FCSTD DOCUMENT  (FreeCAD 0.21R33321 (Git))
Label: 20230531-sunroom-layout
License: All rights reserved
LicenseURL: http://en.wikipedia.org/wiki/All_rights_reserved
objects: Part::Part2DObjectPython×75, Part::FeaturePython×35, App::DocumentObjectGroup×13, App::MeasureDistance×1, Spreadsheet::Sheet×1, App::GeometryPython×1
note: 111 computed .brp shape members not serialized (recipe doc carries the construction recipe); baked Part::Feature solids carry a one-line shape summary decoded from their .brp

FEATURE [Part::Part2DObjectPython] Rectangle001  label="Rect-sec1"  # Draft 2D object (typed FeaturePython)
  Area = 800000
  ChamferSize = 0
  Columns = 1
  FilletRadius = 0
  Height = 400
  Length = 2000
  MakeFace = true
  Placement = pos=(-5613.61,2200,0) rot=(0,0,1;0rad)
  Rows = 1
FEATURE [Part::FeaturePython] Structure001  label="fail"  # Arch/BIM 7 (typed FeaturePython)
  BaseMirror = false
  BaseOffsetX = 0
  BaseOffsetY = 0
  BasePerpendicularToTool = false
  BaseRotation = -21
  ComputedLength = 6000
  FaceMaker = 0
  Height = 64
  HorizontalArea = 4096
  IfcData = attributes={"GlobalId": {"name": "GlobalId", "type": "IfcGloballyUniqueId", "is_enum": false, "enum_values": []}, "Description": {"... (+475 chars omitted),+1 more (map truncated)
  IfcType = 7
  Length = 6000
  MoveBase = false
  MoveWithHost = false
  Nodes = (2) [(-3.54371e-32,-1.11022e-15,8.32667e-16),(6000,-1.11022e-15,8.32667e-16)]
  NodesOffset = 0
  Normal = (0,0,0)
  PerimeterLength = 256
  Placement = pos=(-5368,2460,5000) rot=(0,1,0;1.5708rad)
  PredefinedType = 0
  Profile = IPE120
  ToolOffsetFirst = 0
  ToolOffsetLast = 0
  VerticalArea = 1536000
  Width = 64
  expr: Profile = Spreadsheet.vertcoltype
FEATURE [Part::FeaturePython] Wall  label="NorthWall1-400mm"  # Arch/BIM 166 (typed FeaturePython)
  Align = 2
  Area = 0
  Base = -> Rectangle001
  BlockHeight = 0
  BlockLength = 0
  CountBroken = 0
  CountEntire = 0
  Face = 0
  Height = 3000
  HorizontalArea = 800000
  IfcData = attributes={"GlobalId": {"name": "GlobalId", "type": "IfcGloballyUniqueId", "is_enum": false, "enum_values": []}, "Description": {"... (+533 chars omitted),+1 more (map truncated)
  IfcType = 166
  Joint = 0
  Length = 0
  MakeBlocks = false
  MoveBase = false
  MoveWithHost = false
  Normal = (0,0,0)
  OffsetFirst = 0
  OffsetSecond = 0
  PerimeterLength = 4800
  Placement = pos=(0,0,-600) rot=(0,0,1;0rad)
  PredefinedType = 0
  VerticalArea = 1.44e+07
  Width = 200
FEATURE [App::MeasureDistance] Distance  label="Distance: 2363.01 mm"
  Distance = 2398.43
  P1 = (-3738.2,2140,2600)
  P2 = (-3709.77,2140,4998.26)
FEATURE [Spreadsheet::Sheet] Spreadsheet  label="S"
  cells = A1=BaseHeight; B1(BaseHeight)==5200 mm; A2=BaseLength; B2(BaseLength)==11000 mm; A3=BaseSlabThickness; B3(BaseSlabThickness)==200 mm; A4=ColHeight; B4(ColHeight)==6000 mm; A5=NorthWallThickness; B5(NorthWallThickness)==400 mm; A6=SouthWallThickness; B6(SouthWallThickness)==200 mm; A7=LaundryRoomWidth; B7(LaundryRoomWidth)==3 m; A8=LaundryRoomDepth; B8(LaundryRoomDepth)==3 m; A9=col1xpos; B9(col1xpos)==-BaseLength / 2 + 100 mm; A10=col1ypos; B10(col1ypos)==BaseHeight / 2 - NorthWallThickness / 2; A11=col1xposIPE; B11(col1xposIPE)==col1xpos + 32 mm; A12=col1yposIPE; B12(col1yposIPE)==col1ypos + 60 mm; A13=colwidth; B13(colwidth)==64 mm; A14=colheight; B14(collength)==120 mm; A15=vertcoltype; B15(vertcoltype)=IPE120
FEATURE [Part::Part2DObjectPython] Rectangle003  label="NorthWallRect"  # Draft 2D object (typed FeaturePython)
  Area = 3320000
  ChamferSize = 0
  Columns = 1
  FilletRadius = 0
  Height = 400
  Length = 8300
  MakeFace = true
  Placement = pos=(-5500,2200,0) rot=(0,0,1;0rad)
  Rows = 1
  expr: .Placement.Base.x = -Spreadsheet.BaseLength / 2
  expr: .Placement.Base.y = Spreadsheet.BaseHeight / 2 - Spreadsheet.NorthWallThickness
  expr: Height = Spreadsheet.NorthWallThickness
  expr: Length = Spreadsheet.BaseLength - 3 m + 300 mm
FEATURE [Part::Part2DObjectPython] Rectangle004  label="SouthWallRect"  # Draft 2D object (typed FeaturePython)
  Area = 2200000
  ChamferSize = 0
  Columns = 1
  FilletRadius = 0
  Height = 200
  Length = 11000
  MakeFace = true
  Placement = pos=(-5500,-2600,0) rot=(0,0,1;0rad)
  Rows = 1
  expr: .Placement.Base.x = -Spreadsheet.BaseLength / 2
  expr: .Placement.Base.y = -Spreadsheet.BaseHeight / 2
  expr: Height = Spreadsheet.SouthWallThickness
  expr: Length = Spreadsheet.BaseLength
FEATURE [Part::Part2DObjectPython] Rectangle005  label="NorthColPosRect"  # Draft 2D object (typed FeaturePython)
  Area = 960000
  ChamferSize = 0
  Columns = 1
  FilletRadius = 0
  Height = 120
  Length = 8000
  MakeFace = true
  Placement = pos=(-5500,2400,0) rot=(0,0,1;0rad)
  Rows = 1
  expr: .Placement.Base.x = -Spreadsheet.BaseLength / 2
  expr: .Placement.Base.y = Spreadsheet.BaseHeight / 2 - Spreadsheet.NorthWallThickness / 2
FEATURE [Part::Part2DObjectPython] Rectangle006  label="WestWallRect"  # Draft 2D object (typed FeaturePython)
  Area = 920000
  ChamferSize = 0
  Columns = 1
  FilletRadius = 0
  Height = 4600
  Length = 200
  MakeFace = true
  Placement = pos=(-5500,-2400,0) rot=(0,0,1;0rad)
  Rows = 1
  expr: Height = Spreadsheet.BaseHeight - Spreadsheet.NorthWallThickness - Spreadsheet.SouthWallThickness
  expr: Length = Spreadsheet.SouthWallThickness
FEATURE [Part::Part2DObjectPython] Rectangle007  label="Col1Rect"  # Draft 2D object (typed FeaturePython)
  Area = 7680
  ChamferSize = 0
  Columns = 1
  FilletRadius = 0
  Height = 120
  Length = 64
  MakeFace = true
  Placement = pos=(-5400,2400,0) rot=(0,0,1;0rad)
  Rows = 1
  expr: .Placement.Base.x = Spreadsheet.col1xpos
  expr: .Placement.Base.y = Spreadsheet.col1ypos
  expr: Height = Spreadsheet.collength
  expr: Length = Spreadsheet.colwidth
FEATURE [Part::Part2DObjectPython] Clone2D  label="Col2Rect (2D)"  # Draft 2D object (typed FeaturePython)
  Fuse = false
  Objects = -> [Rectangle007]
  Placement = pos=(-4400,2400,0) rot=(0,0,1;0rad)
  Scale = (1,1,1)
  expr: .Placement.Base.x = Spreadsheet.col1xpos + 1000 mm
  expr: .Placement.Base.y = Spreadsheet.col1ypos
FEATURE [Part::Part2DObjectPython] Clone2D001  label="Col3Rect (2D)"  # Draft 2D object (typed FeaturePython)
  Fuse = false
  Objects = -> [Rectangle007]
  Placement = pos=(-3400,2400,0) rot=(0,0,1;0rad)
  Scale = (1,1,1)
  expr: .Placement.Base.x = Spreadsheet.col1xpos + 2000 mm
FEATURE [Part::Part2DObjectPython] Clone2D002  label="Col4Rect (2D)"  # Draft 2D object (typed FeaturePython)
  Fuse = false
  Objects = -> [Rectangle007]
  Placement = pos=(-2400,2400,0) rot=(0,0,1;0rad)
  Scale = (1,1,1)
  expr: .Placement.Base.x = Spreadsheet.col1xpos + 3000 mm
  expr: .Placement.Base.y = Spreadsheet.col1ypos
FEATURE [Part::Part2DObjectPython] Clone2D003  label="Col5Rect (2D)"  # Draft 2D object (typed FeaturePython)
  Fuse = false
  Objects = -> [Rectangle007]
  Placement = pos=(-1400,2400,0) rot=(0,0,1;0rad)
  Scale = (1,1,1)
  expr: .Placement.Base.x = Spreadsheet.col1xpos + 4000 mm
  expr: .Placement.Base.y = Spreadsheet.col1ypos
FEATURE [Part::Part2DObjectPython] Clone2D004  label="Col7Rect (2D)"  # Draft 2D object (typed FeaturePython)
  Fuse = false
  Objects = -> [Rectangle007]
  Placement = pos=(600,2400,0) rot=(0,0,1;0rad)
  Scale = (1,1,1)
  expr: .Placement.Base.x = Spreadsheet.col1xpos + 6000 mm
  expr: .Placement.Base.y = Spreadsheet.col1ypos
FEATURE [Part::Part2DObjectPython] Clone2D005  label="Col6Rect (2D)"  # Draft 2D object (typed FeaturePython)
  Fuse = false
  Objects = -> [Rectangle007]
  Placement = pos=(-400,2400,0) rot=(0,0,1;0rad)
  Scale = (1,1,1)
  expr: .Placement.Base.x = Spreadsheet.col1xpos + 5000 mm
  expr: .Placement.Base.y = Spreadsheet.col1ypos
FEATURE [Part::Part2DObjectPython] Clone2D006  label="Col8Rect (2D)"  # Draft 2D object (typed FeaturePython)
  Fuse = false
  Objects = -> [Rectangle007]
  Placement = pos=(1600,2400,0) rot=(0,0,1;0rad)
  Scale = (1,1,1)
  expr: .Placement.Base.x = Spreadsheet.col1xpos + 7000 mm
  expr: .Placement.Base.y = Spreadsheet.col1ypos
FEATURE [Part::Part2DObjectPython] Rectangle008  label="LaundryRoomRect"  # Draft 2D object (typed FeaturePython)
  Area = 9000000
  ChamferSize = 0
  Columns = 1
  FilletRadius = 0
  Height = 3000
  Length = 3000
  MakeFace = true
  Placement = pos=(2500,2600,0) rot=(0,0,1;0rad)
  Rows = 1
  expr: .Placement.Base.x = 2500
  expr: Height = Spreadsheet.LaundryRoomDepth
  expr: Length = Spreadsheet.LaundryRoomDepth
FEATURE [Part::Part2DObjectPython] Clone2D007  label="Col9Rect (2D)"  # Draft 2D object (typed FeaturePython)
  Fuse = false
  Objects = -> [Rectangle007]
  Placement = pos=(2602.84,2400.21,0) rot=(0,0,1;0rad)
  Scale = (1,1,1)
FEATURE [App::DocumentObjectGroup] Group001  label="RectN"
  Group = -> [Rectangle007,Clone2D,Clone2D001,Clone2D002,Clone2D003,Clone2D005,Clone2D004,Clone2D006,Clone2D007]
FEATURE [Part::Part2DObjectPython] Clone2D008  label="Col10Rect (2D)"  # Draft 2D object (typed FeaturePython)
  Fuse = false
  Objects = -> [Clone2D007]
  Placement = pos=(2720,3400,0) rot=(0,0,1;1.5708rad)
  Scale = (1,1,1)
  expr: .Placement.Base.x = 2720 mm
  expr: .Placement.Base.y = 2400 mm + 1000 mm
FEATURE [Part::Part2DObjectPython] IPE120005  # Draft 2D object (typed FeaturePython)
  FlangeThickness = 6.3
  Height = 120
  WebThickness = 4.4
  Width = 64
FEATURE [Part::FeaturePython] Structure006  label="Col5"  # Arch/BIM 24 (typed FeaturePython)
  Base = -> IPE120005
  BaseMirror = false
  BaseOffsetX = 0
  BaseOffsetY = 0
  BasePerpendicularToTool = false
  BaseRotation = 0
  ComputedLength = 6000
  FaceMaker = 0
  Height = 6000
  HorizontalArea = 1278.96
  IfcData = attributes={"GlobalId": {"name": "GlobalId", "type": "IfcGloballyUniqueId", "is_enum": false, "enum_values": []}, "Description": {"... (+438 chars omitted),+1 more (map truncated)
  IfcType = 24
  Length = 120
  MoveBase = false
  MoveWithHost = false
  Nodes = (2) [(0,-1.61713e-15,0),(0,-1.61713e-15,6000)]
  NodesOffset = 0
  Normal = (0,0,0)
  PerimeterLength = 487.2
  Placement = pos=(-1368,2460,-1000) rot=(0,0,1;0rad)
  PredefinedType = 0
  Profile = IPE120
  ToolOffsetFirst = 0
  ToolOffsetLast = 0
  VerticalArea = 2923200
  Width = 64
  expr: .Placement.Base.x = Spreadsheet.col1xposIPE + 4000 mm
  expr: .Placement.Base.y = Spreadsheet.col1yposIPE
FEATURE [Part::Part2DObjectPython] IPE120006  # Draft 2D object (typed FeaturePython)
  FlangeThickness = 6.3
  Height = 120
  WebThickness = 4.4
  Width = 64
FEATURE [Part::FeaturePython] Structure007  label="Col6"  # Arch/BIM 24 (typed FeaturePython)
  Base = -> IPE120006
  BaseMirror = false
  BaseOffsetX = 0
  BaseOffsetY = 0
  BasePerpendicularToTool = false
  BaseRotation = 0
  ComputedLength = 6000
  FaceMaker = 0
  Height = 6000
  HorizontalArea = 1278.96
  IfcData = attributes={"GlobalId": {"name": "GlobalId", "type": "IfcGloballyUniqueId", "is_enum": false, "enum_values": []}, "Description": {"... (+438 chars omitted),+1 more (map truncated)
  IfcType = 24
  Length = 120
  MoveBase = false
  MoveWithHost = false
  Nodes = (2) [(0,-1.61713e-15,0),(0,-1.61713e-15,6000)]
  NodesOffset = 0
  Normal = (0,0,0)
  PerimeterLength = 487.2
  Placement = pos=(-368,2460,-1000) rot=(0,0,1;0rad)
  PredefinedType = 0
  Profile = IPE120
  ToolOffsetFirst = 0
  ToolOffsetLast = 0
  VerticalArea = 2923200
  Width = 64
  expr: .Placement.Base.x = Spreadsheet.col1xposIPE + 5000 mm
  expr: .Placement.Base.y = Spreadsheet.col1yposIPE
FEATURE [Part::Part2DObjectPython] IPE120007  # Draft 2D object (typed FeaturePython)
  FlangeThickness = 6.3
  Height = 120
  WebThickness = 4.4
  Width = 64
FEATURE [Part::FeaturePython] Structure008  label="Col7"  # Arch/BIM 24 (typed FeaturePython)
  Base = -> IPE120007
  BaseMirror = false
  BaseOffsetX = 0
  BaseOffsetY = 0
  BasePerpendicularToTool = false
  BaseRotation = 0
  ComputedLength = 6000
  FaceMaker = 0
  Height = 6000
  HorizontalArea = 1278.96
  IfcData = attributes={"GlobalId": {"name": "GlobalId", "type": "IfcGloballyUniqueId", "is_enum": false, "enum_values": []}, "Description": {"... (+438 chars omitted),+1 more (map truncated)
  IfcType = 24
  Length = 120
  MoveBase = false
  MoveWithHost = false
  Nodes = (2) [(0,-1.61713e-15,0),(0,-1.61713e-15,6000)]
  NodesOffset = 0
  Normal = (0,0,0)
  PerimeterLength = 487.2
  Placement = pos=(632,2460,-1000) rot=(0,0,1;0rad)
  PredefinedType = 0
  Profile = IPE120
  ToolOffsetFirst = 0
  ToolOffsetLast = 0
  VerticalArea = 2923200
  Width = 64
  expr: .Placement.Base.x = Spreadsheet.col1xposIPE + 6000 mm
  expr: .Placement.Base.y = Spreadsheet.col1yposIPE
FEATURE [Part::Part2DObjectPython] IPE120008  # Draft 2D object (typed FeaturePython)
  FlangeThickness = 6.3
  Height = 120
  WebThickness = 4.4
  Width = 64
FEATURE [Part::FeaturePython] Structure009  label="Col8"  # Arch/BIM 24 (typed FeaturePython)
  Base = -> IPE120008
  BaseMirror = false
  BaseOffsetX = 0
  BaseOffsetY = 0
  BasePerpendicularToTool = false
  BaseRotation = 0
  ComputedLength = 6000
  FaceMaker = 0
  Height = 6000
  HorizontalArea = 1278.96
  IfcData = attributes={"GlobalId": {"name": "GlobalId", "type": "IfcGloballyUniqueId", "is_enum": false, "enum_values": []}, "Description": {"... (+438 chars omitted),+1 more (map truncated)
  IfcType = 24
  Length = 120
  MoveBase = false
  MoveWithHost = false
  Nodes = (2) [(0,-1.61713e-15,0),(0,-1.61713e-15,6000)]
  NodesOffset = 0
  Normal = (0,0,0)
  PerimeterLength = 487.2
  Placement = pos=(1632,2460,-1000) rot=(0,0,1;0rad)
  PredefinedType = 0
  Profile = IPE120
  ToolOffsetFirst = 0
  ToolOffsetLast = 0
  VerticalArea = 2923200
  Width = 64
  expr: .Placement.Base.x = Spreadsheet.col1xposIPE + 7000 mm
  expr: .Placement.Base.y = Spreadsheet.col1yposIPE
FEATURE [Part::Part2DObjectPython] IPE120009  # Draft 2D object (typed FeaturePython)
  FlangeThickness = 6.3
  Height = 120
  WebThickness = 4.4
  Width = 64
FEATURE [Part::FeaturePython] Structure010  label="Col9"  # Arch/BIM 24 (typed FeaturePython)
  Base = -> IPE120009
  BaseMirror = false
  BaseOffsetX = 0
  BaseOffsetY = 0
  BasePerpendicularToTool = false
  BaseRotation = 0
  ComputedLength = 6000
  FaceMaker = 0
  Height = 6000
  HorizontalArea = 1278.96
  IfcData = attributes={"GlobalId": {"name": "GlobalId", "type": "IfcGloballyUniqueId", "is_enum": false, "enum_values": []}, "Description": {"... (+438 chars omitted),+1 more (map truncated)
  IfcType = 24
  Length = 120
  MoveBase = false
  MoveWithHost = false
  Nodes = (2) [(0,-1.61713e-15,0),(0,-1.61713e-15,6000)]
  NodesOffset = 0
  Normal = (0,0,0)
  PerimeterLength = 487.2
  Placement = pos=(2634.76,2460.15,-1000) rot=(0,0,1;0rad)
  PredefinedType = 0
  Profile = IPE120
  ToolOffsetFirst = 0
  ToolOffsetLast = 0
  VerticalArea = 2923200
  Width = 64
FEATURE [Part::Part2DObjectPython] Rectangle009  label="LaundryWallWestRect"  # Draft 2D object (typed FeaturePython)
  Area = 900000
  ChamferSize = 0
  Columns = 1
  FilletRadius = 0
  Height = 3000
  Length = 300
  MakeFace = true
  Placement = pos=(2500.39,2600,0) rot=(0,0,1;0rad)
  Rows = 1
  expr: Height = Spreadsheet.LaundryRoomDepth
FEATURE [Part::Part2DObjectPython] Clone2D009  label="Col11Rect (2D)"  # Draft 2D object (typed FeaturePython)
  Fuse = false
  Objects = -> [Clone2D008]
  Placement = pos=(2720,4400,0) rot=(0,0,1;1.5708rad)
  Scale = (1,1,1)
  expr: .Placement.Base.y = 2400 mm + 2000 mm
FEATURE [Part::Part2DObjectPython] Clone2D010  label="Col12Rect (2D)"  # Draft 2D object (typed FeaturePython)
  Fuse = false
  Objects = -> [Clone2D009]
  Placement = pos=(2720,5400,0) rot=(0,0,1;1.5708rad)
  Scale = (1,1,1)
  expr: .Placement.Base.y = 2400 mm + 3000 mm
FEATURE [Part::Part2DObjectPython] Rectangle010  label="LaundryWallEastRect"  # Draft 2D object (typed FeaturePython)
  Area = 600000
  ChamferSize = 0
  Columns = 1
  FilletRadius = 0
  Height = 3000
  Length = 200
  MakeFace = true
  Placement = pos=(5300,2600,0) rot=(0,0,1;0rad)
  Rows = 1
  expr: Height = Spreadsheet.LaundryRoomDepth
FEATURE [Part::Part2DObjectPython] Clone2D011  label="Col15Rect (2D)"  # Draft 2D object (typed FeaturePython)
  Fuse = false
  Objects = -> [Clone2D010]
  Placement = pos=(5465.32,5400,0) rot=(0,0,1;1.5708rad)
  Scale = (1,1,1)
FEATURE [Part::Part2DObjectPython] Clone2D012  label="Col16Rect (2D)"  # Draft 2D object (typed FeaturePython)
  Fuse = false
  Objects = -> [Clone2D009]
  Placement = pos=(5465.32,4400,0) rot=(0,0,1;1.5708rad)
  Scale = (1,1,1)
FEATURE [Part::Part2DObjectPython] Clone2D013  label="Col17Rect (2D)"  # Draft 2D object (typed FeaturePython)
  Fuse = false
  Objects = -> [Clone2D008]
  Placement = pos=(5465.32,3400,0) rot=(0,0,1;1.5708rad)
  Scale = (1,1,1)
FEATURE [Part::Part2DObjectPython] Clone2D014  label="Col14Rect (2D)"  # Draft 2D object (typed FeaturePython)
  Fuse = false
  Objects = -> [Clone2D006]
  Placement = pos=(4509.76,5428.53,0) rot=(0,0,1;0rad)
  Scale = (1,1,1)
FEATURE [Part::Part2DObjectPython] Clone2D015  label="Col13Rect (2D)"  # Draft 2D object (typed FeaturePython)
  Fuse = false
  Objects = -> [Clone2D004]
  Placement = pos=(3509.76,5428.53,0) rot=(0,0,1;0rad)
  Scale = (1,1,1)
FEATURE [App::DocumentObjectGroup] Group004  label="Rect"
  Group = -> [Clone2D010,Clone2D009,Clone2D008,Clone2D011,Clone2D012,Clone2D013,Clone2D014,Clone2D015]
FEATURE [Part::Part2DObjectPython] Rectangle011  label="EastWallRect"  # Draft 2D object (typed FeaturePython)
  Area = 1000000
  ChamferSize = 0
  Columns = 1
  FilletRadius = 0
  Height = 5000
  Length = 200
  MakeFace = true
  Placement = pos=(5300,-2400,0) rot=(0,0,1;0rad)
  Rows = 1
FEATURE [App::GeometryPython] BuildingPart  label="Floor"  # Arch/BIM 14 (typed FeaturePython)
  Area = 0
  CompositionType = 0
  Elevation = 0
  Group = -> [Rectangle005,Rectangle011,Rectangle004,Rectangle008,Rectangle009,Rectangle010,Rectangle006]
  Height = 0
  HeightPropagate = true
  IfcData = attributes={"GlobalId": {"name": "GlobalId", "type": "IfcGloballyUniqueId", "is_enum": false, "enum_values": []}, "Description": {"... (+866 chars omitted),+1 more (map truncated)
  IfcType = 14
  LevelOffset = 0
  LongName = Floor
  OnlySolids = true
  expr: Elevation = .Placement.Base.z
FEATURE [Part::Part2DObjectPython] Clone2D016  label="Col18Rect (2D)"  # Draft 2D object (typed FeaturePython)
  Fuse = false
  Objects = -> [Clone2D007]
  Placement = pos=(5460,2400,0) rot=(0,0,1;1.5708rad)
  Scale = (1,1,1)
FEATURE [Part::Part2DObjectPython] IPE120011  # Draft 2D object (typed FeaturePython)
  FlangeThickness = 6.3
  Height = 120
  WebThickness = 4.4
  Width = 64
FEATURE [Part::FeaturePython] Structure011  label="Col13"  # Arch/BIM 24 (typed FeaturePython)
  Base = -> IPE120011
  BaseMirror = false
  BaseOffsetX = 0
  BaseOffsetY = 0
  BasePerpendicularToTool = false
  BaseRotation = 0
  ComputedLength = 6000
  FaceMaker = 0
  Height = 6000
  HorizontalArea = 1278.96
  IfcData = attributes={"GlobalId": {"name": "GlobalId", "type": "IfcGloballyUniqueId", "is_enum": false, "enum_values": []}, "Description": {"... (+438 chars omitted),+1 more (map truncated)
  IfcType = 24
  Length = 120
  MoveBase = false
  MoveWithHost = false
  Nodes = (2) [(0,-1.61713e-15,0),(0,-1.61713e-15,6000)]
  NodesOffset = 0
  Normal = (0,0,0)
  PerimeterLength = 487.2
  Placement = pos=(3541.76,5488.53,-1000) rot=(0,0,-1;0rad)
  PredefinedType = 0
  Profile = IPE120
  ToolOffsetFirst = 0
  ToolOffsetLast = 0
  VerticalArea = 2923200
  Width = 64
FEATURE [Part::Part2DObjectPython] IPE120012  # Draft 2D object (typed FeaturePython)
  FlangeThickness = 6.3
  Height = 120
  WebThickness = 4.4
  Width = 64
FEATURE [Part::FeaturePython] Structure012  label="Col14"  # Arch/BIM 24 (typed FeaturePython)
  Base = -> IPE120012
  BaseMirror = false
  BaseOffsetX = 0
  BaseOffsetY = 0
  BasePerpendicularToTool = false
  BaseRotation = 0
  ComputedLength = 6000
  FaceMaker = 0
  Height = 6000
  HorizontalArea = 1278.96
  IfcData = attributes={"GlobalId": {"name": "GlobalId", "type": "IfcGloballyUniqueId", "is_enum": false, "enum_values": []}, "Description": {"... (+438 chars omitted),+1 more (map truncated)
  IfcType = 24
  Length = 120
  MoveBase = false
  MoveWithHost = false
  Nodes = (2) [(0,-1.61713e-15,0),(0,-1.61713e-15,6000)]
  NodesOffset = 0
  Normal = (0,0,0)
  PerimeterLength = 487.2
  Placement = pos=(4541.76,5488.53,-1000) rot=(0,0,1;0rad)
  PredefinedType = 0
  Profile = IPE120
  ToolOffsetFirst = 0
  ToolOffsetLast = 0
  VerticalArea = 2923200
  Width = 64
FEATURE [Part::Part2DObjectPython] IPE120013  # Draft 2D object (typed FeaturePython)
  FlangeThickness = 6.3
  Height = 120
  WebThickness = 4.4
  Width = 64
FEATURE [Part::FeaturePython] Structure013  label="Col12"  # Arch/BIM 24 (typed FeaturePython)
  Base = -> IPE120013
  BaseMirror = false
  BaseOffsetX = 0
  BaseOffsetY = 0
  BasePerpendicularToTool = false
  BaseRotation = 0
  ComputedLength = 6000
  FaceMaker = 0
  Height = 6000
  HorizontalArea = 1278.96
  IfcData = attributes={"GlobalId": {"name": "GlobalId", "type": "IfcGloballyUniqueId", "is_enum": false, "enum_values": []}, "Description": {"... (+438 chars omitted),+1 more (map truncated)
  IfcType = 24
  Length = 120
  MoveBase = false
  MoveWithHost = false
  Nodes = (2) [(0,-1.61713e-15,0),(0,-1.61713e-15,6000)]
  NodesOffset = 0
  Normal = (0,0,0)
  PerimeterLength = 487.2
  Placement = pos=(2660,5432,-1000) rot=(0,0,1;1.5708rad)
  PredefinedType = 0
  Profile = IPE120
  ToolOffsetFirst = 0
  ToolOffsetLast = 0
  VerticalArea = 2923200
  Width = 64
FEATURE [Part::Part2DObjectPython] IPE120014  # Draft 2D object (typed FeaturePython)
  FlangeThickness = 6.3
  Height = 120
  WebThickness = 4.4
  Width = 64
FEATURE [Part::FeaturePython] Structure014  label="Col11"  # Arch/BIM 24 (typed FeaturePython)
  Base = -> IPE120014
  BaseMirror = false
  BaseOffsetX = 0
  BaseOffsetY = 0
  BasePerpendicularToTool = false
  BaseRotation = 0
  ComputedLength = 6000
  FaceMaker = 0
  Height = 6000
  HorizontalArea = 1278.96
  IfcData = attributes={"GlobalId": {"name": "GlobalId", "type": "IfcGloballyUniqueId", "is_enum": false, "enum_values": []}, "Description": {"... (+438 chars omitted),+1 more (map truncated)
  IfcType = 24
  Length = 120
  MoveBase = false
  MoveWithHost = false
  Nodes = (2) [(0,-1.61713e-15,0),(0,-1.61713e-15,6000)]
  NodesOffset = 0
  Normal = (0,0,0)
  PerimeterLength = 487.2
  Placement = pos=(2660,4432,-1000) rot=(0,0,1;1.5708rad)
  PredefinedType = 0
  Profile = IPE120
  ToolOffsetFirst = 0
  ToolOffsetLast = 0
  VerticalArea = 2923200
  Width = 64
FEATURE [Part::Part2DObjectPython] IPE120015  # Draft 2D object (typed FeaturePython)
  FlangeThickness = 6.3
  Height = 120
  WebThickness = 4.4
  Width = 64
FEATURE [Part::FeaturePython] Structure015  label="Col10"  # Arch/BIM 24 (typed FeaturePython)
  Base = -> IPE120015
  BaseMirror = false
  BaseOffsetX = 0
  BaseOffsetY = 0
  BasePerpendicularToTool = false
  BaseRotation = 0
  ComputedLength = 6000
  FaceMaker = 0
  Height = 6000
  HorizontalArea = 1278.96
  IfcData = attributes={"GlobalId": {"name": "GlobalId", "type": "IfcGloballyUniqueId", "is_enum": false, "enum_values": []}, "Description": {"... (+438 chars omitted),+1 more (map truncated)
  IfcType = 24
  Length = 120
  MoveBase = false
  MoveWithHost = false
  Nodes = (2) [(0,-1.61713e-15,0),(0,-1.61713e-15,6000)]
  NodesOffset = 0
  Normal = (0,0,0)
  PerimeterLength = 487.2
  Placement = pos=(2660,3432,-1000) rot=(0,0,1;1.5708rad)
  PredefinedType = 0
  Profile = IPE120
  ToolOffsetFirst = 0
  ToolOffsetLast = 0
  VerticalArea = 2923200
  Width = 64
FEATURE [Part::Part2DObjectPython] IPE120016  # Draft 2D object (typed FeaturePython)
  FlangeThickness = 6.3
  Height = 120
  WebThickness = 4.4
  Width = 64
FEATURE [Part::FeaturePython] Structure016  label="Col15"  # Arch/BIM 24 (typed FeaturePython)
  Base = -> IPE120016
  BaseMirror = false
  BaseOffsetX = 0
  BaseOffsetY = 0
  BasePerpendicularToTool = false
  BaseRotation = 0
  ComputedLength = 6000
  FaceMaker = 0
  Height = 6000
  HorizontalArea = 1278.96
  IfcData = attributes={"GlobalId": {"name": "GlobalId", "type": "IfcGloballyUniqueId", "is_enum": false, "enum_values": []}, "Description": {"... (+438 chars omitted),+1 more (map truncated)
  IfcType = 24
  Length = 120
  MoveBase = false
  MoveWithHost = false
  Nodes = (2) [(0,-1.61713e-15,0),(0,-1.61713e-15,6000)]
  NodesOffset = 0
  Normal = (0,0,0)
  PerimeterLength = 487.2
  Placement = pos=(5405.32,5432,-1000) rot=(0,0,1;1.5708rad)
  PredefinedType = 0
  Profile = IPE120
  ToolOffsetFirst = 0
  ToolOffsetLast = 0
  VerticalArea = 2923200
  Width = 64
FEATURE [Part::Part2DObjectPython] IPE120017  # Draft 2D object (typed FeaturePython)
  FlangeThickness = 6.3
  Height = 120
  WebThickness = 4.4
  Width = 64
FEATURE [Part::FeaturePython] Structure017  label="Col16"  # Arch/BIM 24 (typed FeaturePython)
  Base = -> IPE120017
  BaseMirror = false
  BaseOffsetX = 0
  BaseOffsetY = 0
  BasePerpendicularToTool = false
  BaseRotation = 0
  ComputedLength = 6000
  FaceMaker = 0
  Height = 6000
  HorizontalArea = 1278.96
  IfcData = attributes={"GlobalId": {"name": "GlobalId", "type": "IfcGloballyUniqueId", "is_enum": false, "enum_values": []}, "Description": {"... (+438 chars omitted),+1 more (map truncated)
  IfcType = 24
  Length = 120
  MoveBase = false
  MoveWithHost = false
  Nodes = (2) [(0,-1.61713e-15,0),(0,-1.61713e-15,6000)]
  NodesOffset = 0
  Normal = (0,0,0)
  PerimeterLength = 487.2
  Placement = pos=(5405.27,4431.98,-1000) rot=(0,0,1;1.5708rad)
  PredefinedType = 0
  Profile = IPE120
  ToolOffsetFirst = 0
  ToolOffsetLast = 0
  VerticalArea = 2923200
  Width = 64
FEATURE [Part::Part2DObjectPython] IPE120018  # Draft 2D object (typed FeaturePython)
  FlangeThickness = 6.3
  Height = 120
  WebThickness = 4.4
  Width = 64
FEATURE [Part::FeaturePython] Structure018  label="Col17"  # Arch/BIM 24 (typed FeaturePython)
  Base = -> IPE120018
  BaseMirror = false
  BaseOffsetX = 0
  BaseOffsetY = 0
  BasePerpendicularToTool = false
  BaseRotation = 0
  ComputedLength = 6000
  FaceMaker = 0
  Height = 6000
  HorizontalArea = 1278.96
  IfcData = attributes={"GlobalId": {"name": "GlobalId", "type": "IfcGloballyUniqueId", "is_enum": false, "enum_values": []}, "Description": {"... (+438 chars omitted),+1 more (map truncated)
  IfcType = 24
  Length = 120
  MoveBase = false
  MoveWithHost = false
  Nodes = (2) [(0,-1.61713e-15,0),(0,-1.61713e-15,6000)]
  NodesOffset = 0
  Normal = (0,0,0)
  PerimeterLength = 487.2
  Placement = pos=(5405.32,3432,-1000) rot=(0,0,1;1.5708rad)
  PredefinedType = 0
  Profile = IPE120
  ToolOffsetFirst = 0
  ToolOffsetLast = 0
  VerticalArea = 2923200
  Width = 64
FEATURE [App::DocumentObjectGroup] Group006  label="ColsLaundry"
  Group = -> [Structure018,Structure011,Structure013,Structure014,Structure017,Structure016,Structure015,Structure012]
FEATURE [App::DocumentObjectGroup] Group005  label="Laundry"
  Group = -> [Group004,Group006]
FEATURE [Part::Part2DObjectPython] Rectangle012  label="LaundryWallNorth"  # Draft 2D object (typed FeaturePython)
  Area = 750000
  ChamferSize = 0
  Columns = 1
  FilletRadius = 0
  Height = 300
  Length = 2500
  MakeFace = true
  Placement = pos=(2800,5300,0) rot=(0,0,1;0rad)
  Rows = 1
FEATURE [Part::Part2DObjectPython] Rectangle013  label="LaundryFloorSlabRect"  # Draft 2D object (typed FeaturePython)
  Area = 6750000
  ChamferSize = 0
  Columns = 1
  FilletRadius = 0
  Height = 2700
  Length = 2500
  MakeFace = true
  Placement = pos=(2802.36,2601.58,0) rot=(0,0,1;0rad)
  Rows = 1
FEATURE [Part::Part2DObjectPython] IPE120019  # Draft 2D object (typed FeaturePython)
  FlangeThickness = 6.3
  Height = 120
  WebThickness = 4.4
  Width = 64
FEATURE [Part::FeaturePython] Structure019  label="Col18"  # Arch/BIM 24 (typed FeaturePython)
  Base = -> IPE120019
  BaseMirror = false
  BaseOffsetX = 0
  BaseOffsetY = 0
  BasePerpendicularToTool = false
  BaseRotation = 0
  ComputedLength = 6000
  FaceMaker = 0
  Height = 6000
  HorizontalArea = 1278.96
  IfcData = attributes={"GlobalId": {"name": "GlobalId", "type": "IfcGloballyUniqueId", "is_enum": false, "enum_values": []}, "Description": {"... (+438 chars omitted),+1 more (map truncated)
  IfcType = 24
  Length = 120
  MoveBase = false
  MoveWithHost = false
  Nodes = (2) [(0,-1.61713e-15,0),(0,-1.61713e-15,6000)]
  NodesOffset = 0
  Normal = (0,0,0)
  PerimeterLength = 487.2
  Placement = pos=(5400,2432,-1000) rot=(0,0,1;1.5708rad)
  PredefinedType = 0
  Profile = IPE120
  ToolOffsetFirst = 0
  ToolOffsetLast = 0
  VerticalArea = 2923200
  Width = 64
FEATURE [Part::Part2DObjectPython] Clone2D017  label="Col31Rect"  # Draft 2D object (typed FeaturePython)
  Fuse = false
  Objects = -> [Rectangle007]
  Placement = pos=(-5400,-2557.73,0) rot=(0,0,1;0rad)
  Scale = (1,1,1)
  expr: .Placement.Base.x = Spreadsheet.col1xpos
FEATURE [Part::Part2DObjectPython] Clone2D018  label="Col30Rect"  # Draft 2D object (typed FeaturePython)
  Fuse = false
  Objects = -> [Clone2D]
  Placement = pos=(-4400,-2557.73,0) rot=(0,0,1;0rad)
  Scale = (1,1,1)
  expr: .Placement.Base.x = Spreadsheet.col1xpos + 1000 mm
FEATURE [Part::Part2DObjectPython] Clone2D019  label="Col29Rect"  # Draft 2D object (typed FeaturePython)
  Fuse = false
  Objects = -> [Clone2D001]
  Placement = pos=(-3400,-2557.73,0) rot=(0,0,1;0rad)
  Scale = (1,1,1)
  expr: .Placement.Base.x = Spreadsheet.col1xpos + 2000 mm
FEATURE [Part::Part2DObjectPython] Clone2D020  label="Col28Rect"  # Draft 2D object (typed FeaturePython)
  Fuse = false
  Objects = -> [Clone2D002]
  Placement = pos=(-2400,-2557.73,0) rot=(0,0,1;0rad)
  Scale = (1,1,1)
  expr: .Placement.Base.x = Spreadsheet.col1xpos + 3000 mm
FEATURE [Part::Part2DObjectPython] Clone2D021  label="Col27Rect"  # Draft 2D object (typed FeaturePython)
  Fuse = false
  Objects = -> [Clone2D003]
  Placement = pos=(-1400,-2557.73,0) rot=(0,0,1;0rad)
  Scale = (1,1,1)
  expr: .Placement.Base.x = Spreadsheet.col1xpos + 4000 mm
FEATURE [Part::Part2DObjectPython] Clone2D022  label="Col26Rect"  # Draft 2D object (typed FeaturePython)
  Fuse = false
  Objects = -> [Clone2D005]
  Placement = pos=(-400,-2557.73,0) rot=(0,0,1;0rad)
  Scale = (1,1,1)
  expr: .Placement.Base.x = Spreadsheet.col1xpos + 5000 mm
FEATURE [Part::Part2DObjectPython] Clone2D023  label="Col25Rect"  # Draft 2D object (typed FeaturePython)
  Fuse = false
  Objects = -> [Clone2D004]
  Placement = pos=(570.338,-2557.73,0) rot=(0,0,1;0rad)
  Scale = (1,1,1)
FEATURE [Part::Part2DObjectPython] Clone2D025  label="Col24Rect"  # Draft 2D object (typed FeaturePython)
  Fuse = false
  Objects = -> [Clone2D020]
  Placement = pos=(1599.92,-2557.73,0) rot=(0,0,1;0rad)
  Scale = (1,1,1)
FEATURE [Part::Part2DObjectPython] Clone2D026  label="Col23Rect"  # Draft 2D object (typed FeaturePython)
  Fuse = false
  Objects = -> [Clone2D021]
  Placement = pos=(2599.92,-2557.73,0) rot=(0,0,1;0rad)
  Scale = (1,1,1)
FEATURE [Part::Part2DObjectPython] Clone2D027  label="Col22Rect"  # Draft 2D object (typed FeaturePython)
  Fuse = false
  Objects = -> [Clone2D022]
  Placement = pos=(3599.92,-2557.73,0) rot=(0,0,1;0rad)
  Scale = (1,1,1)
FEATURE [Part::Part2DObjectPython] Clone2D028  label="Col21Rect"  # Draft 2D object (typed FeaturePython)
  Fuse = false
  Objects = -> [Clone2D023]
  Placement = pos=(4570.26,-2557.73,0) rot=(0,0,1;0rad)
  Scale = (1,1,1)
FEATURE [Part::Part2DObjectPython] Clone2D029  label="Col20Rect"  # Draft 2D object (typed FeaturePython)
  Fuse = false
  Placement = pos=(5460.05,-2532.3,0) rot=(0,0,1;1.5708rad)
  Scale = (1,1,1)
FEATURE [Part::Part2DObjectPython] Clone2D030  label="Col19Rect"  # Draft 2D object (typed FeaturePython)
  Fuse = false
  Objects = -> [Clone2D016]
  Placement = pos=(5460,0,0) rot=(0,0,1;1.5708rad)
  Scale = (1,1,1)
FEATURE [Part::Part2DObjectPython] Clone2D031  label="Col32Rect"  # Draft 2D object (typed FeaturePython)
  Fuse = false
  Objects = -> [Clone2D030]
  Placement = pos=(-5340,0,0) rot=(0,0,1;1.5708rad)
  Scale = (1,1,1)
FEATURE [App::DocumentObjectGroup] Group008  label="RectS"
  Group = -> [Clone2D017,Clone2D018,Clone2D019,Clone2D020,Clone2D021,Clone2D022,Clone2D023,Clone2D025,Clone2D026,Clone2D027,Clone2D028,Clone2D031]
FEATURE [App::DocumentObjectGroup] Group002  label="South"
  Group = -> [Group008]
FEATURE [Part::Part2DObjectPython] IPE120020  # Draft 2D object (typed FeaturePython)
  FlangeThickness = 6.3
  Height = 120
  WebThickness = 4.4
  Width = 64
FEATURE [Part::FeaturePython] Structure020  label="Col29"  # Arch/BIM 24 (typed FeaturePython)
  Base = -> IPE120020
  BaseMirror = false
  BaseOffsetX = 0
  BaseOffsetY = 0
  BasePerpendicularToTool = false
  BaseRotation = 0
  ComputedLength = 6000
  FaceMaker = 0
  Height = 6000
  HorizontalArea = 1278.96
  IfcData = attributes={"GlobalId": {"name": "GlobalId", "type": "IfcGloballyUniqueId", "is_enum": false, "enum_values": []}, "Description": {"... (+438 chars omitted),+1 more (map truncated)
  IfcType = 24
  Length = 120
  MoveBase = false
  MoveWithHost = false
  Nodes = (2) [(0,-1.61713e-15,0),(0,-1.61713e-15,6000)]
  NodesOffset = 0
  Normal = (0,0,0)
  PerimeterLength = 487.2
  Placement = pos=(-3368,-2497.73,-1000) rot=(0,0,1;0rad)
  PredefinedType = 0
  Profile = IPE120
  ToolOffsetFirst = 0
  ToolOffsetLast = 0
  VerticalArea = 2923200
  Width = 64
FEATURE [Part::Part2DObjectPython] IPE120021  # Draft 2D object (typed FeaturePython)
  FlangeThickness = 6.3
  Height = 120
  WebThickness = 4.4
  Width = 64
FEATURE [Part::FeaturePython] Structure021  label="Col27"  # Arch/BIM 24 (typed FeaturePython)
  Base = -> IPE120021
  BaseMirror = false
  BaseOffsetX = 0
  BaseOffsetY = 0
  BasePerpendicularToTool = false
  BaseRotation = 0
  ComputedLength = 6000
  FaceMaker = 0
  Height = 6000
  HorizontalArea = 1278.96
  IfcData = attributes={"GlobalId": {"name": "GlobalId", "type": "IfcGloballyUniqueId", "is_enum": false, "enum_values": []}, "Description": {"... (+438 chars omitted),+1 more (map truncated)
  IfcType = 24
  Length = 120
  MoveBase = false
  MoveWithHost = false
  Nodes = (2) [(0,-1.61713e-15,0),(0,-1.61713e-15,6000)]
  NodesOffset = 0
  Normal = (0,0,0)
  PerimeterLength = 487.2
  Placement = pos=(-1368,-2497.65,-1000) rot=(0,0,1;0rad)
  PredefinedType = 0
  Profile = IPE120
  ToolOffsetFirst = 0
  ToolOffsetLast = 0
  VerticalArea = 2923200
  Width = 64
FEATURE [Part::Part2DObjectPython] IPE120022  # Draft 2D object (typed FeaturePython)
  FlangeThickness = 6.3
  Height = 120
  WebThickness = 4.4
  Width = 64
FEATURE [Part::FeaturePython] Structure022  label="Col25"  # Arch/BIM 24 (typed FeaturePython)
  Base = -> IPE120022
  BaseMirror = false
  BaseOffsetX = 0
  BaseOffsetY = 0
  BasePerpendicularToTool = false
  BaseRotation = 0
  ComputedLength = 6000
  FaceMaker = 0
  Height = 6000
  HorizontalArea = 1278.96
  IfcData = attributes={"GlobalId": {"name": "GlobalId", "type": "IfcGloballyUniqueId", "is_enum": false, "enum_values": []}, "Description": {"... (+438 chars omitted),+1 more (map truncated)
  IfcType = 24
  Length = 120
  MoveBase = false
  MoveWithHost = false
  Nodes = (2) [(0,-1.61713e-15,0),(0,-1.61713e-15,6000)]
  NodesOffset = 0
  Normal = (0,0,0)
  PerimeterLength = 487.2
  Placement = pos=(630.27,-2497.92,-1000) rot=(0,0,1;0rad)
  PredefinedType = 0
  Profile = IPE120
  ToolOffsetFirst = 0
  ToolOffsetLast = 0
  VerticalArea = 2923200
  Width = 64
FEATURE [Part::Part2DObjectPython] IPE120023  # Draft 2D object (typed FeaturePython)
  FlangeThickness = 6.3
  Height = 120
  WebThickness = 4.4
  Width = 64
FEATURE [Part::FeaturePython] Structure023  label="Col23"  # Arch/BIM 24 (typed FeaturePython)
  Base = -> IPE120023
  BaseMirror = false
  BaseOffsetX = 0
  BaseOffsetY = 0
  BasePerpendicularToTool = false
  BaseRotation = 0
  ComputedLength = 6000
  FaceMaker = 0
  Height = 6000
  HorizontalArea = 1278.96
  IfcData = attributes={"GlobalId": {"name": "GlobalId", "type": "IfcGloballyUniqueId", "is_enum": false, "enum_values": []}, "Description": {"... (+438 chars omitted),+1 more (map truncated)
  IfcType = 24
  Length = 120
  MoveBase = false
  MoveWithHost = false
  Nodes = (2) [(0,-1.61713e-15,0),(0,-1.61713e-15,6000)]
  NodesOffset = 0
  Normal = (0,0,0)
  PerimeterLength = 487.2
  Placement = pos=(2631.92,-2497.73,-1000) rot=(0,0,1;0rad)
  PredefinedType = 0
  Profile = IPE120
  ToolOffsetFirst = 0
  ToolOffsetLast = 0
  VerticalArea = 2923200
  Width = 64
FEATURE [Part::Part2DObjectPython] IPE120024  # Draft 2D object (typed FeaturePython)
  FlangeThickness = 6.3
  Height = 120
  WebThickness = 4.4
  Width = 64
FEATURE [Part::FeaturePython] Structure024  label="Col19"  # Arch/BIM 24 (typed FeaturePython)
  Base = -> IPE120024
  BaseMirror = false
  BaseOffsetX = 0
  BaseOffsetY = 0
  BasePerpendicularToTool = false
  BaseRotation = 0
  ComputedLength = 6000
  FaceMaker = 0
  Height = 6000
  HorizontalArea = 1278.96
  IfcData = attributes={"GlobalId": {"name": "GlobalId", "type": "IfcGloballyUniqueId", "is_enum": false, "enum_values": []}, "Description": {"... (+438 chars omitted),+1 more (map truncated)
  IfcType = 24
  Length = 120
  MoveBase = false
  MoveWithHost = false
  Nodes = (2) [(0,-1.61713e-15,0),(0,-1.61713e-15,6000)]
  NodesOffset = 0
  Normal = (0,0,0)
  PerimeterLength = 487.2
  Placement = pos=(5400,32,-1000) rot=(0,0,1;1.5708rad)
  PredefinedType = 0
  Profile = IPE120
  ToolOffsetFirst = 0
  ToolOffsetLast = 0
  VerticalArea = 2923200
  Width = 64
FEATURE [App::DocumentObjectGroup] Group010  label="ColE"
  Group = -> [Structure024]
FEATURE [App::DocumentObjectGroup] Group011  label="RectE"
  Group = -> [Clone2D029,Clone2D030]
FEATURE [App::DocumentObjectGroup] Group009  label="East"
  Group = -> [Group010,Group011]
FEATURE [Part::Part2DObjectPython] IPE120025  # Draft 2D object (typed FeaturePython)
  FlangeThickness = 6.3
  Height = 120
  WebThickness = 4.4
  Width = 64
FEATURE [Part::FeaturePython] Structure025  label="Col31"  # Arch/BIM 24 (typed FeaturePython)
  Base = -> IPE120025
  BaseMirror = false
  BaseOffsetX = 0
  BaseOffsetY = 0
  BasePerpendicularToTool = false
  BaseRotation = 0
  ComputedLength = 6000
  FaceMaker = 0
  Height = 6000
  HorizontalArea = 1278.96
  IfcData = attributes={"GlobalId": {"name": "GlobalId", "type": "IfcGloballyUniqueId", "is_enum": false, "enum_values": []}, "Description": {"... (+438 chars omitted),+1 more (map truncated)
  IfcType = 24
  Length = 120
  MoveBase = false
  MoveWithHost = false
  Nodes = (2) [(0,-1.61713e-15,0),(0,-1.61713e-15,6000)]
  NodesOffset = 0
  Normal = (0,0,0)
  PerimeterLength = 487.2
  Placement = pos=(-5368,-2497.73,-1000) rot=(0,0,1;0rad)
  PredefinedType = 0
  Profile = IPE120
  ToolOffsetFirst = 0
  ToolOffsetLast = 0
  VerticalArea = 2923200
  Width = 64
FEATURE [Part::Part2DObjectPython] IPE120026  # Draft 2D object (typed FeaturePython)
  FlangeThickness = 6.3
  Height = 120
  WebThickness = 4.4
  Width = 64
FEATURE [Part::FeaturePython] Structure026  label="Col32"  # Arch/BIM 24 (typed FeaturePython)
  Base = -> IPE120026
  BaseMirror = false
  BaseOffsetX = 0
  BaseOffsetY = 0
  BasePerpendicularToTool = false
  BaseRotation = 0
  ComputedLength = 6000
  FaceMaker = 0
  Height = 6000
  HorizontalArea = 1278.96
  IfcData = attributes={"GlobalId": {"name": "GlobalId", "type": "IfcGloballyUniqueId", "is_enum": false, "enum_values": []}, "Description": {"... (+438 chars omitted),+1 more (map truncated)
  IfcType = 24
  Length = 120
  MoveBase = false
  MoveWithHost = false
  Nodes = (2) [(0,-1.61713e-15,0),(0,-1.61713e-15,6000)]
  NodesOffset = 0
  Normal = (0,0,0)
  PerimeterLength = 487.2
  Placement = pos=(-5400,32,-1000) rot=(0,0,1;1.5708rad)
  PredefinedType = 0
  Profile = IPE120
  ToolOffsetFirst = 0
  ToolOffsetLast = 0
  VerticalArea = 2923200
  Width = 64
FEATURE [Part::Part2DObjectPython] IPE120028  # Draft 2D object (typed FeaturePython)
  FlangeThickness = 8.5
  Height = 200
  WebThickness = 5.6
  Width = 100
FEATURE [Part::FeaturePython] Structure028  label="Beam2-IPE200"  # Arch/BIM 7 (typed FeaturePython)
  Base = -> IPE120028
  BaseMirror = false
  BaseOffsetX = 0
  BaseOffsetY = 0
  BasePerpendicularToTool = false
  BaseRotation = 0
  ComputedLength = 4838
  FaceMaker = 0
  Height = 4838
  HorizontalArea = 940507
  IfcData = attributes={"GlobalId": {"name": "GlobalId", "type": "IfcGloballyUniqueId", "is_enum": false, "enum_values": []}, "Description": {"... (+475 chars omitted),+1 more (map truncated)
  IfcType = 7
  Length = 200
  MoveBase = false
  MoveWithHost = false
  Nodes = (2) [(0,-1.95917e-14,0),(0,-1.95917e-14,4838)]
  NodesOffset = 0
  Normal = (0,0,0)
  PerimeterLength = 0
  Placement = pos=(-1368.82,2400.24,2500) rot=(1,0,0;1.5708rad)
  PredefinedType = 0
  Profile = IPE200
  ToolOffsetFirst = 0
  ToolOffsetLast = 0
  VerticalArea = 1.94065e+06
  Width = 100
FEATURE [Part::Part2DObjectPython] IPE120029  # Draft 2D object (typed FeaturePython)
  FlangeThickness = 8.5
  Height = 200
  WebThickness = 5.6
  Width = 100
FEATURE [Part::FeaturePython] Structure029  label="Beam4-IPE200"  # Arch/BIM 7 (typed FeaturePython)
  Base = -> IPE120029
  BaseMirror = false
  BaseOffsetX = 0
  BaseOffsetY = 0
  BasePerpendicularToTool = false
  BaseRotation = 0
  ComputedLength = 4838
  FaceMaker = 0
  Height = 4838
  HorizontalArea = 940507
  IfcData = attributes={"GlobalId": {"name": "GlobalId", "type": "IfcGloballyUniqueId", "is_enum": false, "enum_values": []}, "Description": {"... (+475 chars omitted),+1 more (map truncated)
  IfcType = 7
  Length = 200
  MoveBase = false
  MoveWithHost = false
  Nodes = (2) [(0,-1.95917e-14,0),(0,-1.95917e-14,4838)]
  NodesOffset = 0
  Normal = (0,0,0)
  PerimeterLength = 0
  Placement = pos=(2634.93,2400.2,2500) rot=(1,0,0;1.5708rad)
  PredefinedType = 0
  Profile = IPE200
  ToolOffsetFirst = 0
  ToolOffsetLast = 0
  VerticalArea = 1.94065e+06
  Width = 100
FEATURE [Part::FeaturePython] Wall002  label="NorthWall"  # Arch/BIM 166 (typed FeaturePython)
  Align = 2
  Area = 0
  Base = -> Rectangle003
  BlockHeight = 0
  BlockLength = 0
  CountBroken = 0
  CountEntire = 0
  Face = 0
  Height = 2900
  HorizontalArea = 3320000
  IfcData = attributes={"GlobalId": {"name": "GlobalId", "type": "IfcGloballyUniqueId", "is_enum": false, "enum_values": []}, "Description": {"... (+533 chars omitted),+1 more (map truncated)
  IfcType = 166
  Joint = 0
  Length = 0
  MakeBlocks = false
  MoveBase = false
  MoveWithHost = false
  Normal = (0,0,0)
  OffsetFirst = 0
  OffsetSecond = 0
  PerimeterLength = 17400
  PredefinedType = 0
  VerticalArea = 50460000
  Width = 200
FEATURE [Part::FeaturePython] Wall003  label="Wall"  # Arch/BIM 166 (typed FeaturePython)
  Align = 2
  Area = 0
  Base = -> Rectangle009
  BlockHeight = 0
  BlockLength = 0
  CountBroken = 0
  CountEntire = 0
  Face = 0
  Height = 3000
  HorizontalArea = 900000
  IfcData = attributes={"GlobalId": {"name": "GlobalId", "type": "IfcGloballyUniqueId", "is_enum": false, "enum_values": []}, "Description": {"... (+533 chars omitted),+1 more (map truncated)
  IfcType = 166
  Joint = 0
  Length = 0
  MakeBlocks = false
  MoveBase = false
  MoveWithHost = false
  Normal = (0,0,0)
  OffsetFirst = 0
  OffsetSecond = 0
  PerimeterLength = 6600
  Placement = pos=(0,0,-500) rot=(0,0,1;0rad)
  PredefinedType = 0
  VerticalArea = 19800000
  Width = 200
FEATURE [Part::Part2DObjectPython] IPE200001  # Draft 2D object (typed FeaturePython)
  FlangeThickness = 8.5
  Height = 200
  WebThickness = 5.6
  Width = 100
FEATURE [Part::FeaturePython] Structure  label="Beam5"  # Arch/BIM 24 (typed FeaturePython)
  Base = -> IPE200001
  BaseMirror = false
  BaseOffsetX = 0
  BaseOffsetY = 0
  BasePerpendicularToTool = false
  BaseRotation = 0
  ComputedLength = 1930
  FaceMaker = 0
  Height = 1930
  HorizontalArea = 375192
  IfcData = attributes={"GlobalId": {"name": "GlobalId", "type": "IfcGloballyUniqueId", "is_enum": false, "enum_values": []}, "Description": {"... (+438 chars omitted),+1 more (map truncated)
  IfcType = 24
  Length = 200
  MoveBase = false
  MoveWithHost = false
  Nodes = (2) [(0,-1.95917e-14,0),(0,-1.95917e-14,1930)]
  NodesOffset = 0
  Normal = (0,0,0)
  PerimeterLength = 0
  Placement = pos=(-5340,29.43,2500) rot=(0.57735,0.57735,0.57735;2.0944rad)
  PredefinedType = 0
  Profile = IPE200
  ToolOffsetFirst = 0
  ToolOffsetLast = 0
  VerticalArea = 777450
  Width = 100
FEATURE [Part::Part2DObjectPython] IPE200002  # Draft 2D object (typed FeaturePython)
  FlangeThickness = 8.5
  Height = 200
  WebThickness = 5.6
  Width = 100
FEATURE [Part::FeaturePython] Structure030  label="Beam6"  # Arch/BIM 24 (typed FeaturePython)
  Base = -> IPE200002
  BaseMirror = false
  BaseOffsetX = 0
  BaseOffsetY = 0
  BasePerpendicularToTool = false
  BaseRotation = 0
  ComputedLength = 2700
  FaceMaker = 0
  Height = 2700
  HorizontalArea = 524880
  IfcData = attributes={"GlobalId": {"name": "GlobalId", "type": "IfcGloballyUniqueId", "is_enum": false, "enum_values": []}, "Description": {"... (+438 chars omitted),+1 more (map truncated)
  IfcType = 24
  Length = 200
  MoveBase = false
  MoveWithHost = false
  Nodes = (2) [(0,-1.95917e-14,0),(0,-1.95917e-14,2700)]
  NodesOffset = 0
  Normal = (0,0,0)
  PerimeterLength = 0
  Placement = pos=(5340,10.71,2500) rot=(0.57735,-0.57735,-0.57735;2.0944rad)
  PredefinedType = 0
  Profile = IPE200
  ToolOffsetFirst = 0
  ToolOffsetLast = 0
  VerticalArea = 1.08545e+06
  Width = 100
FEATURE [Part::Part2DObjectPython] Rectangle  label="Base"  # Draft 2D object (typed FeaturePython)
  Area = 57200000
  ChamferSize = 0
  Columns = 1
  FilletRadius = 0
  Height = 5200
  Length = 11000
  MakeFace = true
  Placement = pos=(-5500,-2600,0) rot=(0,0,1;0rad)
  Rows = 1
  expr: .Placement.Base.x = -Spreadsheet.BaseLength / 2
  expr: .Placement.Base.y = -Spreadsheet.BaseHeight / 2
  expr: Height = Spreadsheet.BaseHeight
  expr: Length = Spreadsheet.BaseLength
FEATURE [Part::Part2DObjectPython] IPE120004  # Draft 2D object (typed FeaturePython)
  FlangeThickness = 6.3
  Height = 120
  WebThickness = 4.4
  Width = 64
FEATURE [Part::FeaturePython] Structure005  label="Col4"  # Arch/BIM 7 (typed FeaturePython)
  Base = -> IPE120004
  BaseMirror = false
  BaseOffsetX = 0
  BaseOffsetY = 0
  BasePerpendicularToTool = false
  BaseRotation = 0
  ComputedLength = 6000
  FaceMaker = 0
  Height = 6000
  HorizontalArea = 1278.96
  IfcData = attributes={"GlobalId": {"name": "GlobalId", "type": "IfcGloballyUniqueId", "is_enum": false, "enum_values": []}, "Description": {"... (+475 chars omitted),+1 more (map truncated)
  IfcType = 7
  Length = 120
  MoveBase = false
  MoveWithHost = false
  Nodes = (2) [(0,-1.61713e-15,0),(0,-1.61713e-15,6000)]
  NodesOffset = 0
  Normal = (0,0,0)
  PerimeterLength = 487.2
  Placement = pos=(-2368,2460,-1000) rot=(0,0,1;0rad)
  PredefinedType = 0
  Profile = IPE120
  ToolOffsetFirst = 0
  ToolOffsetLast = 0
  VerticalArea = 2923200
  Width = 64
  expr: .Placement.Base.x = Spreadsheet.col1xposIPE + 3000 mm
  expr: .Placement.Base.y = Spreadsheet.col1yposIPE
  expr: Height = Spreadsheet.ColHeight
FEATURE [Part::Part2DObjectPython] IPE120027  label="IPE2003"  # Draft 2D object (typed FeaturePython)
  FlangeThickness = 8.5
  Height = 200
  WebThickness = 5.6
  Width = 100
FEATURE [Part::FeaturePython] Structure027  label="Beam3-IPE200"  # Arch/BIM 7 (typed FeaturePython)
  Base = -> IPE120027
  BaseMirror = false
  BaseOffsetX = 0
  BaseOffsetY = 0
  BasePerpendicularToTool = false
  BaseRotation = 0
  ComputedLength = 4838
  FaceMaker = 0
  Height = 4838
  HorizontalArea = 940507
  IfcData = attributes={"GlobalId": {"name": "GlobalId", "type": "IfcGloballyUniqueId", "is_enum": false, "enum_values": []}, "Description": {"... (+475 chars omitted),+1 more (map truncated)
  IfcType = 7
  Length = 200
  MoveBase = false
  MoveWithHost = false
  Nodes = (2) [(0,-1.95917e-14,0),(0,-1.95917e-14,4838)]
  NodesOffset = 0
  Normal = (0,0,0)
  PerimeterLength = 0
  Placement = pos=(633.192,2400.06,2500) rot=(1,0,0;1.5708rad)
  PredefinedType = 0
  Profile = IPE200
  ToolOffsetFirst = 0
  ToolOffsetLast = 0
  VerticalArea = 1.94065e+06
  Width = 100
FEATURE [Part::Part2DObjectPython] IPE120003  # Draft 2D object (typed FeaturePython)
  FlangeThickness = 6.3
  Height = 120
  WebThickness = 4.4
  Width = 64
FEATURE [Part::FeaturePython] Structure004  label="Col3"  # Arch/BIM 7 (typed FeaturePython)
  Base = -> IPE120003
  BaseMirror = false
  BaseOffsetX = 0
  BaseOffsetY = 0
  BasePerpendicularToTool = false
  BaseRotation = 0
  ComputedLength = 6000
  FaceMaker = 0
  Height = 6000
  HorizontalArea = 1278.96
  IfcData = attributes={"GlobalId": {"name": "GlobalId", "type": "IfcGloballyUniqueId", "is_enum": false, "enum_values": []}, "Description": {"... (+475 chars omitted),+1 more (map truncated)
  IfcType = 7
  Length = 120
  MoveBase = false
  MoveWithHost = false
  Nodes = (2) [(0,-1.61713e-15,0),(0,-1.61713e-15,6000)]
  NodesOffset = 0
  Normal = (0,0,0)
  PerimeterLength = 487.2
  Placement = pos=(-3368,2460,-1000) rot=(0,0,1;0rad)
  PredefinedType = 0
  Profile = IPE120
  ToolOffsetFirst = 0
  ToolOffsetLast = 0
  VerticalArea = 2923200
  Width = 64
  expr: .Placement.Base.x = Spreadsheet.col1xposIPE + 2000 mm
  expr: .Placement.Base.y = Spreadsheet.col1yposIPE
  expr: Height = Spreadsheet.ColHeight
FEATURE [Part::Part2DObjectPython] IPE120002  # Draft 2D object (typed FeaturePython)
  FlangeThickness = 6.3
  Height = 120
  WebThickness = 4.4
  Width = 64
FEATURE [Part::FeaturePython] Structure003  label="Col2"  # Arch/BIM 7 (typed FeaturePython)
  Base = -> IPE120002
  BaseMirror = false
  BaseOffsetX = 0
  BaseOffsetY = 0
  BasePerpendicularToTool = false
  BaseRotation = 0
  ComputedLength = 6000
  FaceMaker = 0
  Height = 6000
  HorizontalArea = 1278.96
  IfcData = attributes={"GlobalId": {"name": "GlobalId", "type": "IfcGloballyUniqueId", "is_enum": false, "enum_values": []}, "Description": {"... (+475 chars omitted),+1 more (map truncated)
  IfcType = 7
  Length = 120
  MoveBase = false
  MoveWithHost = false
  Nodes = (2) [(0,-1.61713e-15,0),(0,-1.61713e-15,6000)]
  NodesOffset = 0
  Normal = (0,0,0)
  PerimeterLength = 487.2
  Placement = pos=(-4368,2460,-1000) rot=(0,0,1;0rad)
  PredefinedType = 0
  Profile = IPE120
  ToolOffsetFirst = 0
  ToolOffsetLast = 0
  VerticalArea = 2923200
  Width = 64
  expr: .Placement.Base.x = Spreadsheet.col1xposIPE + 1000 mm
  expr: .Placement.Base.y = Spreadsheet.col1yposIPE
  expr: Height = Spreadsheet.ColHeight
FEATURE [App::DocumentObjectGroup] Group003  label="ColsN"
  Group = -> [Structure001,Structure003,Structure004,Structure005,Structure006,Structure007,Structure008,Structure009,Structure010]
FEATURE [App::DocumentObjectGroup] Group007  label="North"
  Group = -> [Group001,Group003]
FEATURE [App::DocumentObjectGroup] Group  label="Columns"
  Group = -> [Group002,Group005,Group007,Group009]
FEATURE [Part::Part2DObjectPython] IPE200  # Draft 2D object (typed FeaturePython)
  FlangeThickness = 8.5
  Height = 200
  WebThickness = 5.6
  Width = 100
FEATURE [Part::FeaturePython] Structure002  label="Beam1-IPE200"  # Arch/BIM 7 (typed FeaturePython)
  Base = -> IPE200
  BaseMirror = false
  BaseOffsetX = 0
  BaseOffsetY = 0
  BasePerpendicularToTool = false
  BaseRotation = 0
  ComputedLength = 4838
  FaceMaker = 0
  Height = 4838
  HorizontalArea = 940507
  IfcData = attributes={"GlobalId": {"name": "GlobalId", "type": "IfcGloballyUniqueId", "is_enum": false, "enum_values": []}, "Description": {"... (+475 chars omitted),+1 more (map truncated)
  IfcType = 7
  Length = 200
  MoveBase = false
  MoveWithHost = false
  Nodes = (2) [(0,-1.95917e-14,0),(0,-1.95917e-14,4838)]
  NodesOffset = 0
  Normal = (0,0,0)
  PerimeterLength = 0
  Placement = pos=(-3367.32,2400,2500) rot=(1,0,0;1.5708rad)
  PredefinedType = 0
  Profile = IPE200
  ToolOffsetFirst = 0
  ToolOffsetLast = 0
  VerticalArea = 1.94065e+06
  Width = 100
FEATURE [App::DocumentObjectGroup] Group012  label="Beams"
  Group = -> [Structure027,Structure028,Structure029,Structure002]
FEATURE [Part::Part2DObjectPython] IPE200003  # Draft 2D object (typed FeaturePython)
  FlangeThickness = 8.5
  Height = 200
  WebThickness = 5.6
  Width = 100
FEATURE [Part::FeaturePython] Structure031  label="Column"  # Arch/BIM 24 (typed FeaturePython)
  Base = -> IPE200003
  BaseMirror = false
  BaseOffsetX = 0
  BaseOffsetY = 0
  BasePerpendicularToTool = false
  BaseRotation = 0
  ComputedLength = 1900
  FaceMaker = 0
  Height = 1900
  HorizontalArea = 369360
  IfcData = attributes={"GlobalId": {"name": "GlobalId", "type": "IfcGloballyUniqueId", "is_enum": false, "enum_values": []}, "Description": {"... (+438 chars omitted),+1 more (map truncated)
  IfcType = 24
  Length = 200
  MoveBase = false
  MoveWithHost = false
  Nodes = (2) [(0,-1.95917e-14,0),(0,-1.95917e-14,1900)]
  NodesOffset = 0
  Normal = (0,0,0)
  PerimeterLength = 0
  Placement = pos=(-3318.08,28.0682,2.48852e+16) rot=(0.57735,0.57735,0.57735;2.0944rad)
  PredefinedType = 0
  Profile = IPE200
  ToolOffsetFirst = 0
  ToolOffsetLast = 0
  VerticalArea = 765450
  Width = 100
